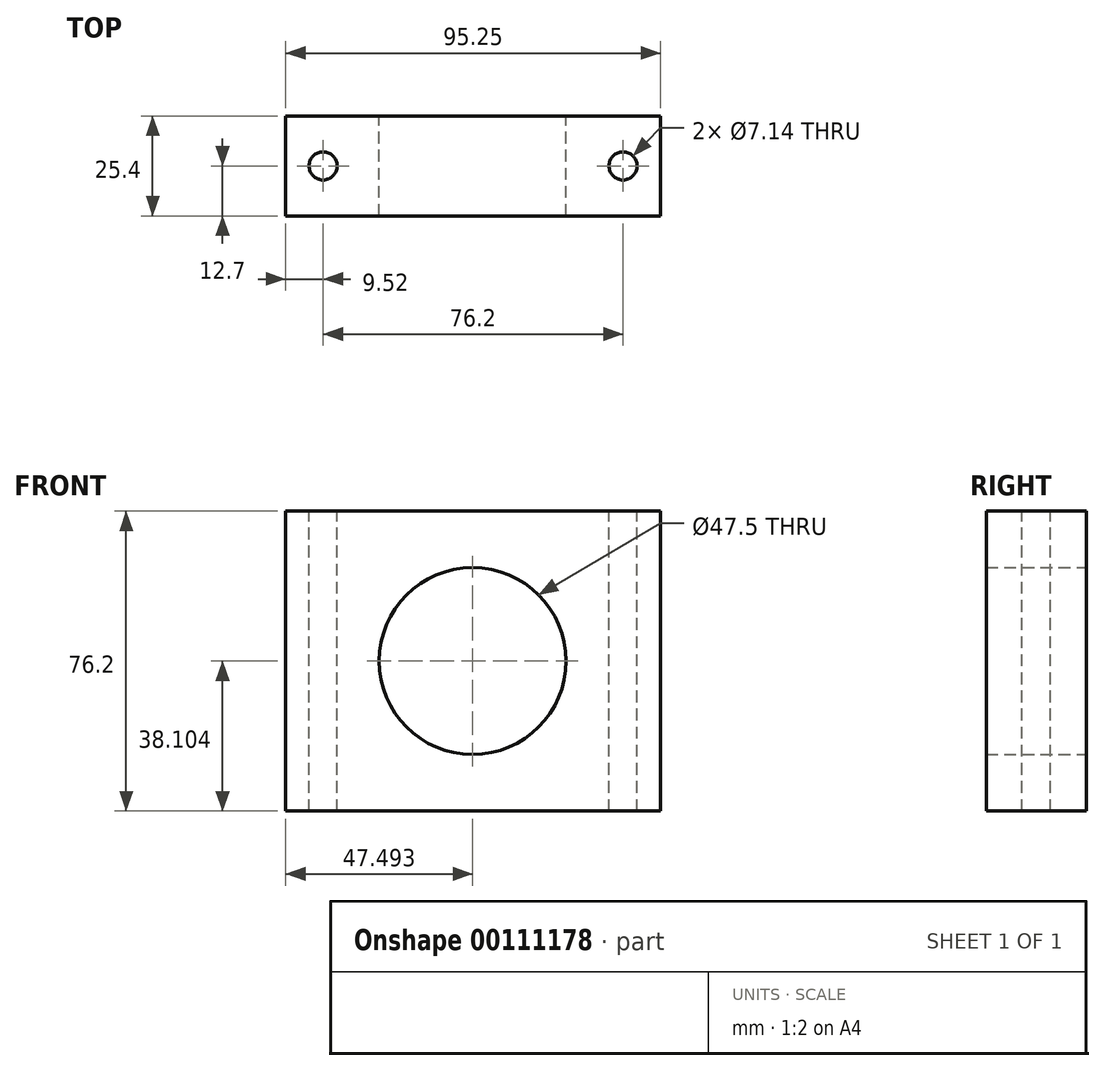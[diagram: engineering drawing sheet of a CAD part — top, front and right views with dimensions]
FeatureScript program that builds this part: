
annotation { "Feature Type Name" : "Feature", "Feature Type Description" : "" }
export const myFeature = defineFeature(function(context is Context, id is Id, definition is map)
    precondition{}
    {
        {
            var Q0;
            Q0=qCreatedBy(makeId("Front.planeOp"),FACE);
            var sketch = newSketch(context, id + "F0", { "sketchPlane" : qUnion([Q0])});
            skLineSegment(sketch, "E0", {"start": v(-47.75, -34.26) * mm, "end": v(47.5, -34.26) * mm});
            skLineSegment(sketch, "E1", {"start": v(47.5, -34.26) * mm, "end": v(47.5, 41.94) * mm});
            skLineSegment(sketch, "E2", {"start": v(47.5, 41.94) * mm, "end": v(-47.75, 41.94) * mm});
            skLineSegment(sketch, "E3", {"start": v(-47.75, 41.94) * mm, "end": v(-47.75, -34.26) * mm});
            skCircle(sketch, "E4", {"center": v(-0.26, 3.84) * mm, "radius": 23.75 * mm});
            skSolve(sketch);
        }
        {
            var Q0;
            Q0 = qSketchRegion(id + "F0", true);
            extrude(context, id + "F1", {"entities" : qUnion([Q0]), "depth" : 25.4 * mm});
        }
        {
            var Q0;
            Q0=makeQuery(id+"F1.opExtrude","SWEPT_FACE",FACE,{"disambiguationData":[OSD([sQuery(id+"F0.wireOp",EDGE,"E2")])]});
            var sketch = newSketch(context, id + "F2", { "sketchPlane" : qUnion([Q0])});
            skCircle(sketch, "E5", {"center": v(-38.23, -12.7) * mm, "radius": 3.57 * mm});
            skCircle(sketch, "E6", {"center": v(37.97, -12.7) * mm, "radius": 3.57 * mm});
            skSolve(sketch);
        }
        {
            var Q0;
            Q0 = qSketchRegion(id + "F2", true);
            extrude(context, id + "F3", {"entities" : qUnion([Q0]), "operationType" : NewBodyOperationType.REMOVE, "endBound" : BoundingType.THROUGH_ALL, "oppositeDirection" : true, "depth" : 25.4 * mm});
        }
    });
